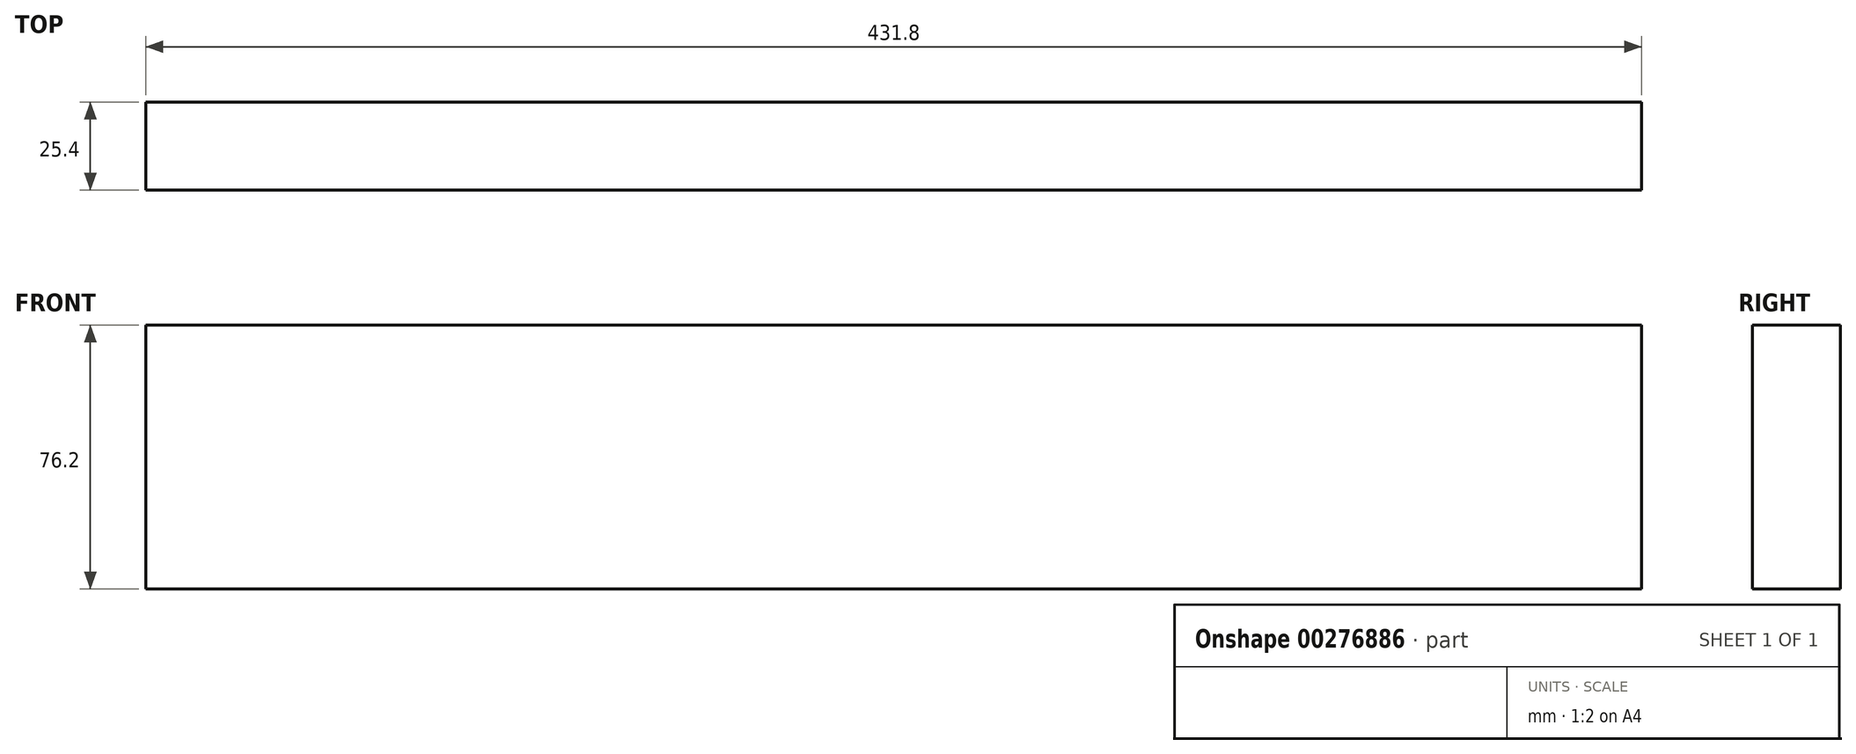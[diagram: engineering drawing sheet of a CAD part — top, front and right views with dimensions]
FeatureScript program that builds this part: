
annotation { "Feature Type Name" : "Feature", "Feature Type Description" : "" }
export const myFeature = defineFeature(function(context is Context, id is Id, definition is map)
    precondition{}
    {
        {
            var Q0;
            Q0=qCreatedBy(makeId("Front.planeOp"),FACE);
            var sketch = newSketch(context, id + "F0", { "sketchPlane" : qUnion([Q0])});
            skLineSegment(sketch, "E0.bottom", {"start": v(0, 0) * mm, "end": v(431.8, 0) * mm});
            skLineSegment(sketch, "E0.top", {"start": v(0, 76.2) * mm, "end": v(431.8, 76.2) * mm});
            skLineSegment(sketch, "E0.left", {"start": v(0, 0) * mm, "end": v(0, 76.2) * mm});
            skLineSegment(sketch, "E0.right", {"start": v(431.8, 0) * mm, "end": v(431.8, 76.2) * mm});
            skSolve(sketch);
        }
        {
            var Q0;
            Q0=makeQuery(id+"F0.imprint","IMPRINT",FACE,{"disambiguationData":[TD([[makeQuery(id+"F0.imprint","IMPRINT",EDGE,{"derivedFrom":sQuery(id+"F0.wireOp",EDGE,"E0.bottom")}),1.0]])]});
            extrude(context, id + "F1", {"entities" : qUnion([Q0]), "depth" : 25.4 * mm});
        }
    });
